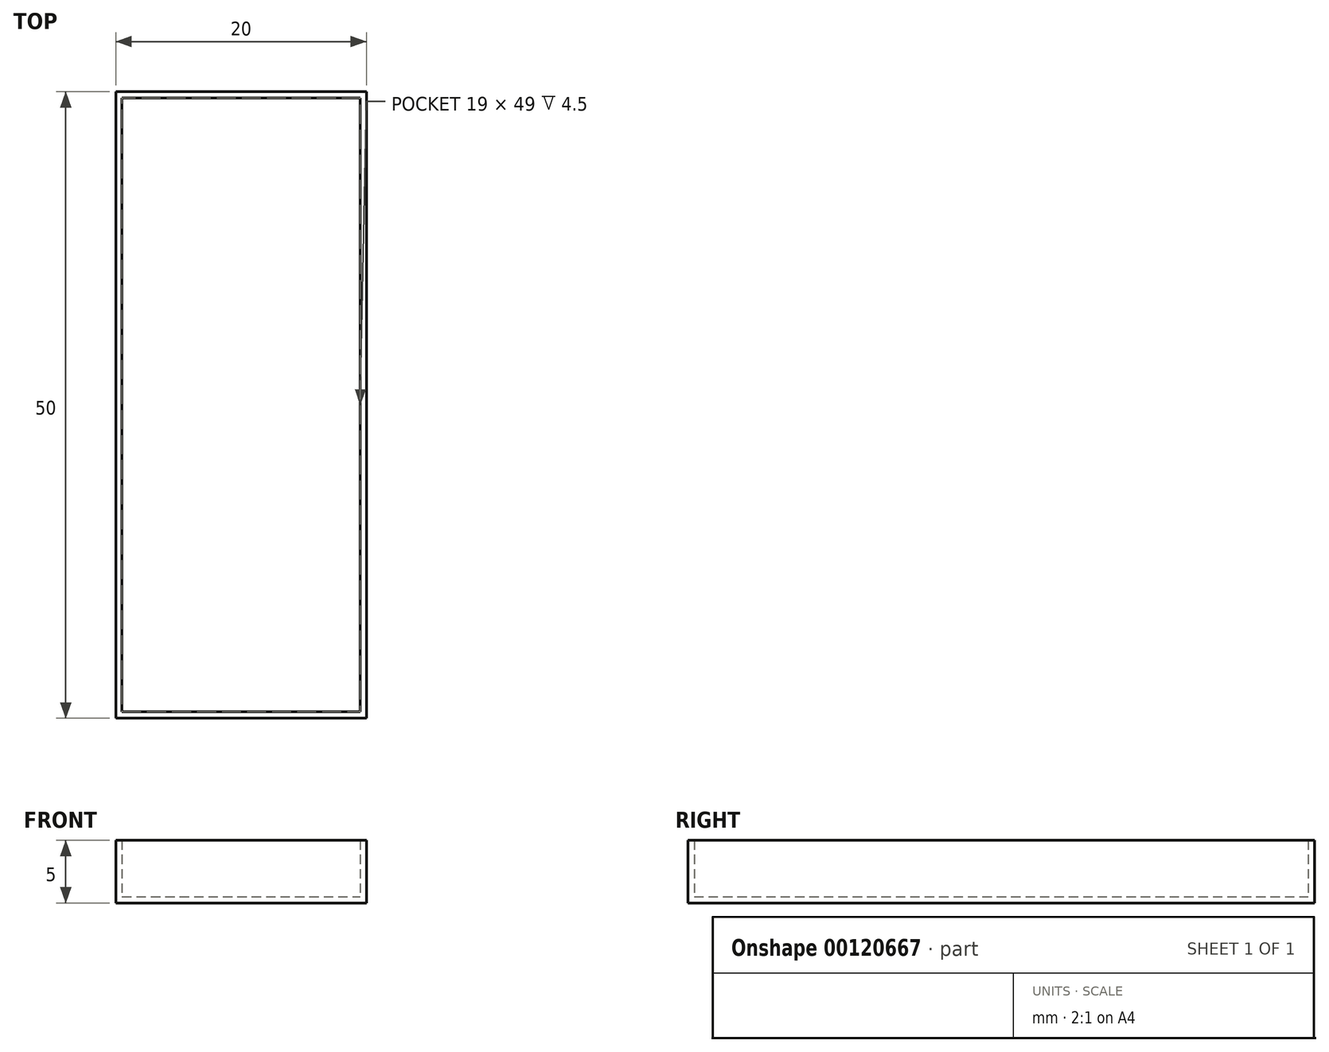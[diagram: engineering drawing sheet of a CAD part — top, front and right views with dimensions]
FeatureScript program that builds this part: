
annotation { "Feature Type Name" : "Feature", "Feature Type Description" : "" }
export const myFeature = defineFeature(function(context is Context, id is Id, definition is map)
    precondition{}
    {
        {
            var Q0;
            Q0=qCreatedBy(makeId("Top.planeOp"),FACE);
            var sketch = newSketch(context, id + "F0", { "sketchPlane" : qUnion([Q0])});
            skLineSegment(sketch, "E0", {"start": v(-10, 25) * mm, "end": v(10, 25) * mm});
            skLineSegment(sketch, "E1", {"start": v(10, 25) * mm, "end": v(10, -25) * mm});
            skLineSegment(sketch, "E2", {"start": v(10, -25) * mm, "end": v(-10, -25) * mm});
            skLineSegment(sketch, "E3", {"start": v(-10, -25) * mm, "end": v(-10, 25) * mm});
            skSolve(sketch);
        }
        {
            var Q0;
            Q0=makeQuery(id+"F0.imprint","IMPRINT",FACE,{"disambiguationData":[TD([[makeQuery(id+"F0.imprint","IMPRINT",EDGE,{"derivedFrom":sQuery(id+"F0.wireOp",EDGE,"E0")}),-1.0]])]});
            extrude(context, id + "F1", {"entities" : qUnion([Q0]), "depth" : 5 * mm});
        }
        {
            var Q0;
            Q0=makeQuery(id+"F1.opExtrude","CAP_FACE",FACE,{"disambiguationData":[OSD([sQuery(id+"F0.wireOp",EDGE,"E0"),sQuery(id+"F0.wireOp",EDGE,"E1"),sQuery(id+"F0.wireOp",EDGE,"E2"),sQuery(id+"F0.wireOp",EDGE,"E3")])],"isStart":false});
            shell(context, id + "F2", {"entities" : qUnion([Q0]), "thickness" : 0.5 * mm});
        }
    });
